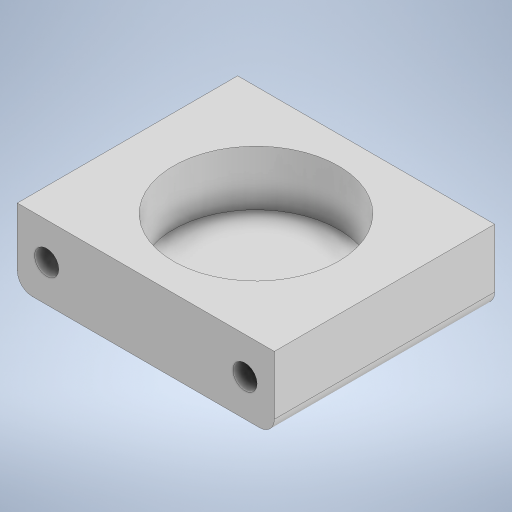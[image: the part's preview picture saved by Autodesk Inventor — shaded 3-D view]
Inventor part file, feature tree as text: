
AUTODESK INVENTOR PART (.ipt)
format: ipt  version: 2023 (Build 270158000, 158)  size: 239,104 bytes
history: native  units: in
note: dims shown in document units (in); Inventor stores cm internally (conversion verified against a paired STEP export)
features: extrude x3, sketch x3, fillet x1
ambient origin geometry x8: Origin, YZ Plane, XZ Plane, XY Plane, X Axis, Y Axis, Z Axis, Center Point
bodies: Solid1 (feature_tree)
feature tree (7):
  extrude  "Extrusion1"  Depth=0.3937in
  extrude  "Extrusion2"  Depth=1.1811in
  extrude  "Extrusion3"  Depth=0.0787in
  fillet  "Fillet2"  Radius=0.1575in
  sketch  "Sketch1"  dims[d0=1.378in d1=0.3937in]
  sketch  "Sketch2"  dims[d2=1.1811in d3=0.0in d5=0.8858in]
  sketch  "Sketch3"  dims[d6=0.2953in d7=0.0in d8=0.1299in d9=0.1575in d10=0.1575in d11=0.3937in d12=0.0in d13=0.0787in]
